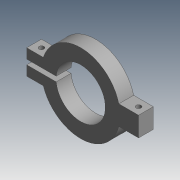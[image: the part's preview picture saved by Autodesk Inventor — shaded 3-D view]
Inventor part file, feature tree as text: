
AUTODESK INVENTOR PART (.ipt)
format: ipt  version: 2015 (Build 190159000, 159)  size: 120,832 bytes
history: native  units: mm
features: extrude x3, sketch x3
ambient origin geometry x8: Origin, YZ Plane, XZ Plane, XY Plane, X Axis, Y Axis, Z Axis, Center Point
bodies: Solid1 (feature_tree)
feature tree (6):
  extrude  "Extrusion1"  Depth=160.0mm
  extrude  "Extrusion2"  Depth=20.0mm
  extrude  "Extrusion3"  Depth=10.0mm
  sketch  "Sketch1"  dims[d0=100.0mm d1=160.0mm]
  sketch  "Sketch3"  dims[d4=5.0mm d5=20.0mm]
  sketch  "Sketch4"  dims[d6=30.0mm d7=0.0mm d8=10.0mm d9=15.0mm d10=15.0mm d11=30.0mm d12=0.0mm d13=20.0mm d14=40.0mm d15=10.0mm d16=15.0mm d17=15.0mm d18=30.0mm d19=0.0mm d20=60.0mm]
